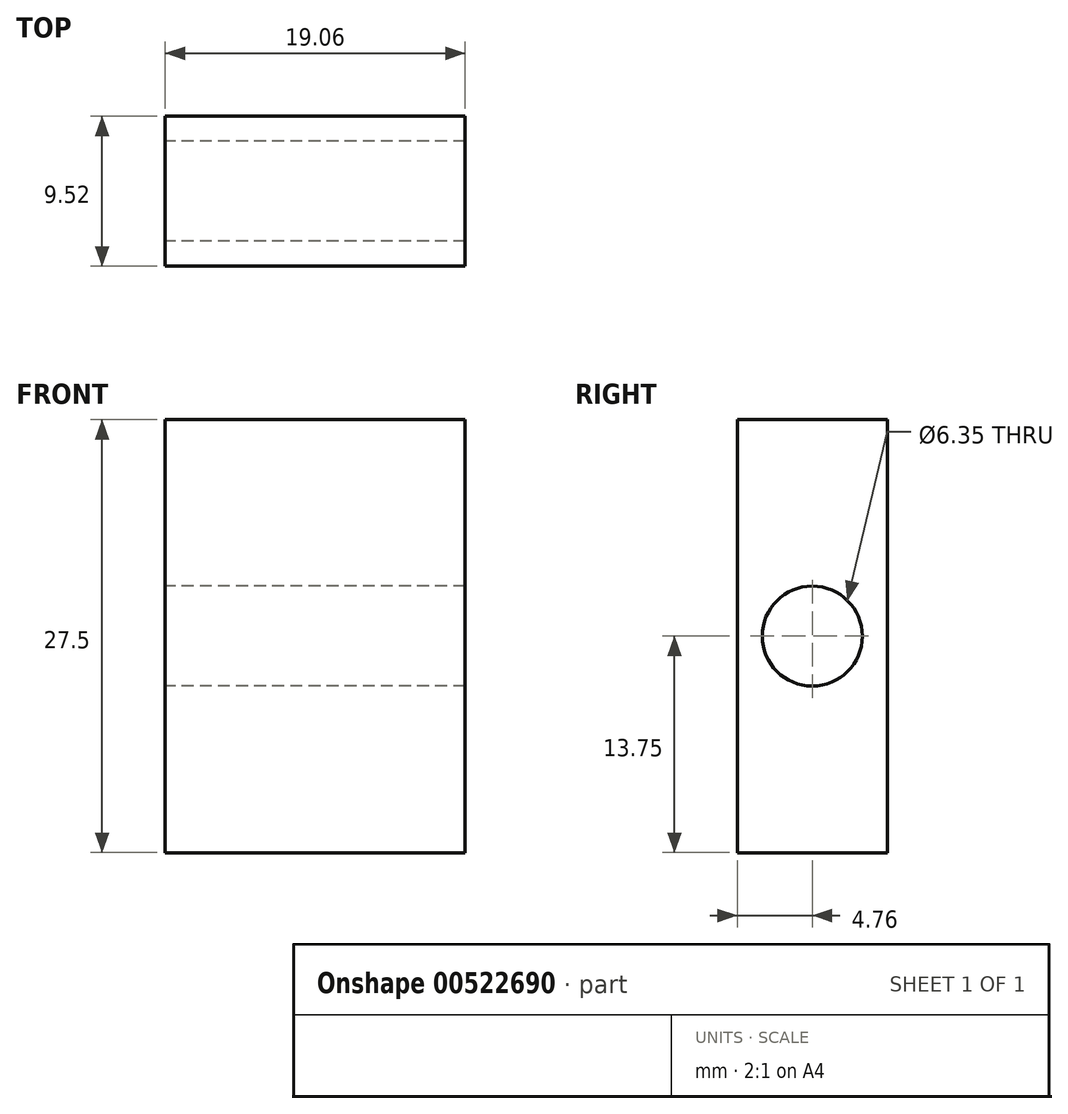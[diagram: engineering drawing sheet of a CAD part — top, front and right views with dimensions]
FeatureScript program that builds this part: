
annotation { "Feature Type Name" : "Feature", "Feature Type Description" : "" }
export const myFeature = defineFeature(function(context is Context, id is Id, definition is map)
    precondition{}
    {
        {
            var Q0;
            Q0=qCreatedBy(makeId("Right.planeOp"),FACE);
            var sketch = newSketch(context, id + "F0", { "sketchPlane" : qUnion([Q0])});
            skLineSegment(sketch, "E0.bottom", {"start": v(-4.76, -13.75) * mm, "end": v(4.76, -13.75) * mm});
            skLineSegment(sketch, "E0.top", {"start": v(-4.76, 13.75) * mm, "end": v(4.76, 13.75) * mm});
            skLineSegment(sketch, "E0.left", {"start": v(-4.76, -13.75) * mm, "end": v(-4.76, 13.75) * mm});
            skLineSegment(sketch, "E0.right", {"start": v(4.76, -13.75) * mm, "end": v(4.76, 13.75) * mm});
            skPoint(sketch, "E0.middle", {"position": v(0, 0) * mm});
            skCircle(sketch, "E1", {"center": v(0, 0) * mm, "radius": 3.18 * mm});
            skSolve(sketch);
        }
        {
            var Q0;
            Q0 = qSketchRegion(id + "F0", true);
            extrude(context, id + "F1", {"entities" : qUnion([Q0]), "endBound" : BoundingType.SYMMETRIC, "depth" : 19.05 * mm, "offsetDistance" : 25.4 * mm});
        }
    });
